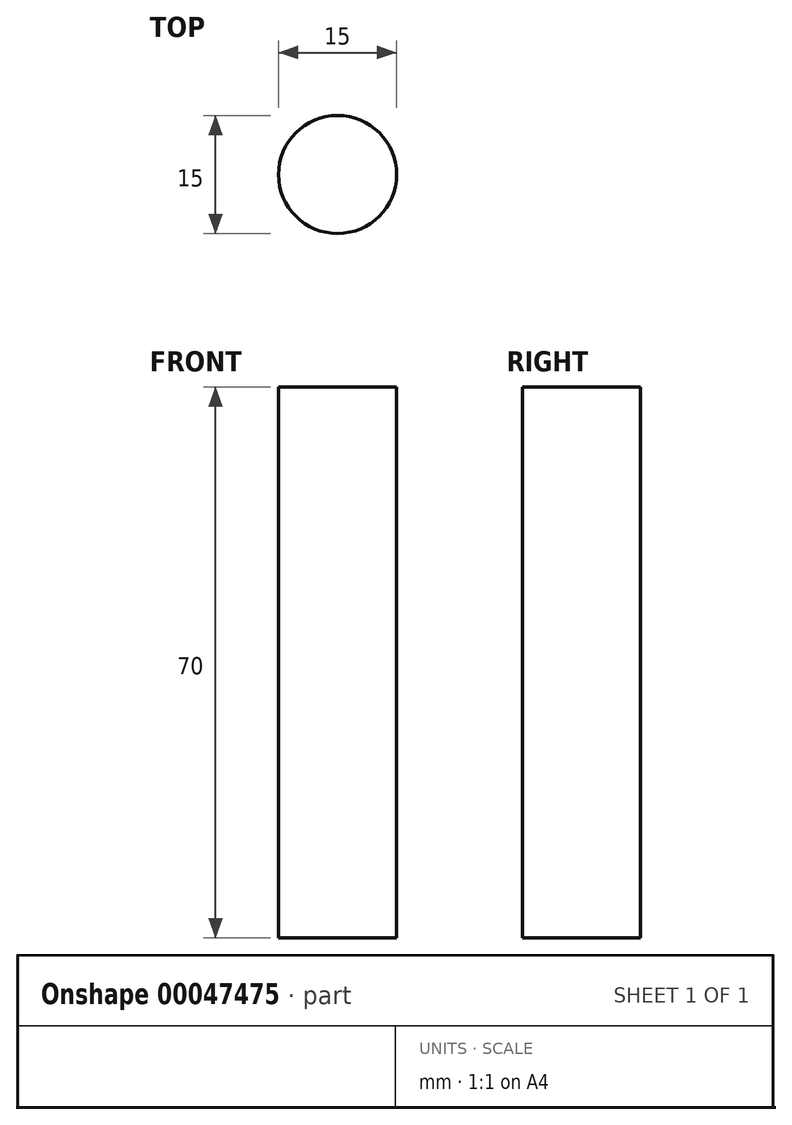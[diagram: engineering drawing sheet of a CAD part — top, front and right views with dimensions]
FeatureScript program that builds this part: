
annotation { "Feature Type Name" : "Feature", "Feature Type Description" : "" }
export const myFeature = defineFeature(function(context is Context, id is Id, definition is map)
    precondition{}
    {
        {
            var Q0;
            Q0=qCreatedBy(makeId("Top.planeOp"),FACE);
            var sketch = newSketch(context, id + "F0", { "sketchPlane" : qUnion([Q0])});
            skCircle(sketch, "E0", {"center": v(0, 0) * mm, "radius": 7.5 * mm});
            skSolve(sketch);
        }
        {
            var Q0;
            Q0 = qSketchRegion(id + "F0", true);
            extrude(context, id + "F1", {"entities" : qUnion([Q0]), "depth" : 70 * mm});
        }
    });
